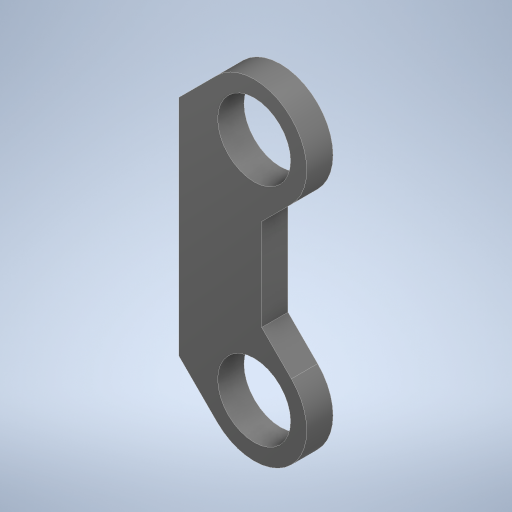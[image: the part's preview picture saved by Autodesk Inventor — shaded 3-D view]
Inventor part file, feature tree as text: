
AUTODESK INVENTOR PART (.ipt)
format: ipt  version: 2024.3 (Build 283343000, 343)  size: 268,800 bytes
history: native  units: in
note: dims shown in document units (in); Inventor stores cm internally (conversion verified against a paired STEP export)
features: extrude x1, sketch x1, other x1
ambient origin geometry x8: Origin, YZ Plane, XZ Plane, XY Plane, X Axis, Y Axis, Z Axis, Center Point
bodies: Solid1 (feature_tree)
feature tree (3):
  extrude  "Extrusion1"  [1 undecoded]
  sketch  "Sketch1"  dims[d0=0.0in d1=0.0in]
  other  "Saliente-Extruir3"
note: 1 required parameter value undecoded (feature->parameter linkage not recoverable at this tier; creation-order binding heuristic only, values carry confidence <= 0.55)
